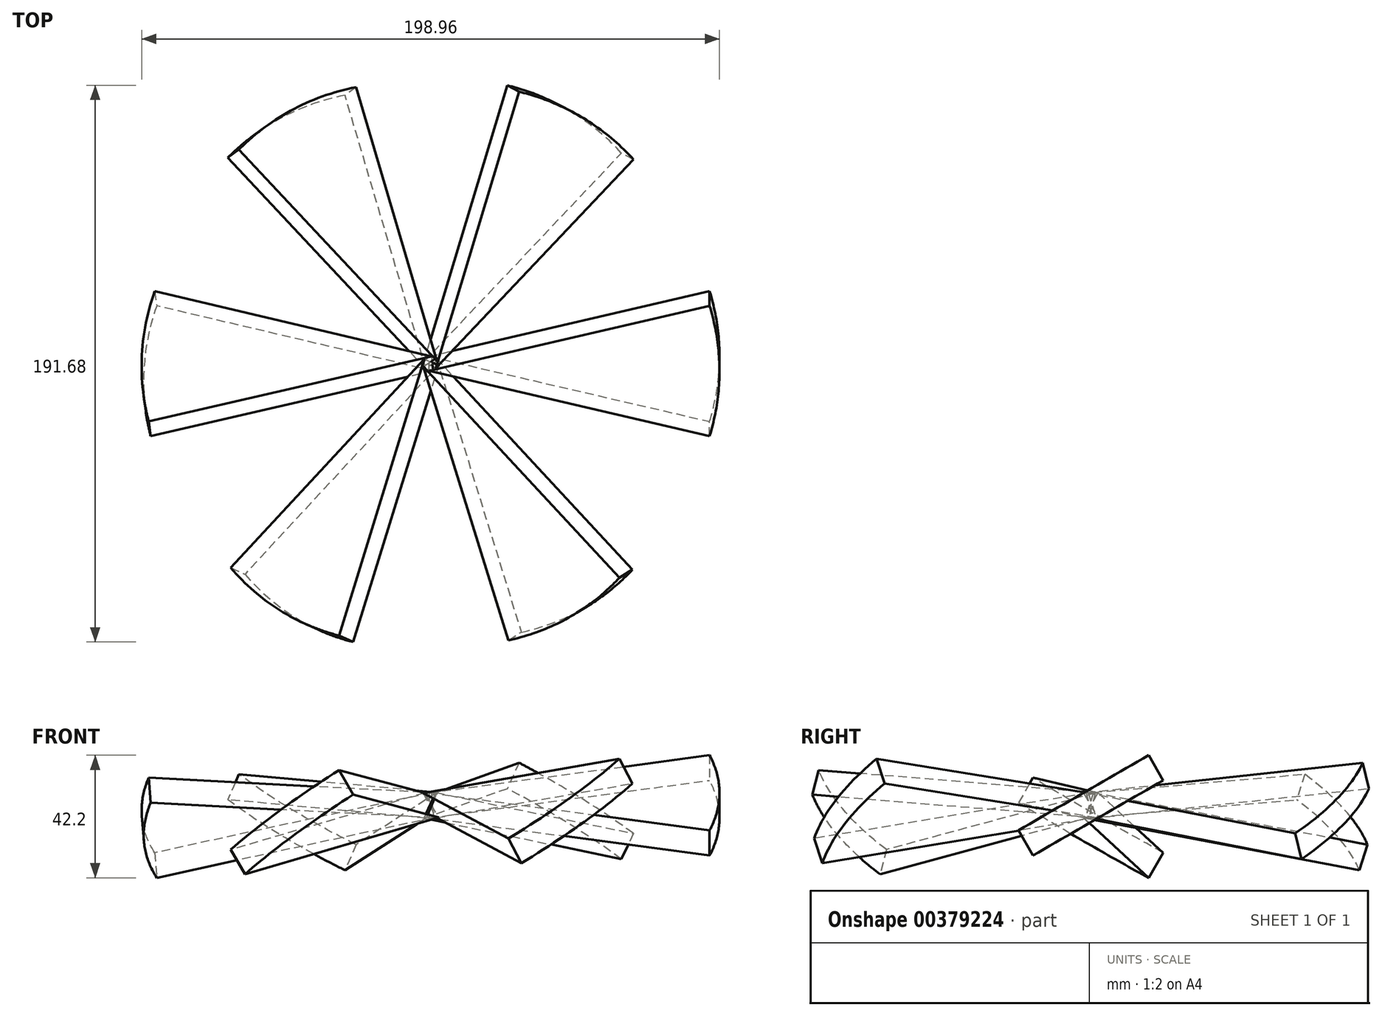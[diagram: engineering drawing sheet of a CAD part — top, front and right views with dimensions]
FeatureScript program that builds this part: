
annotation { "Feature Type Name" : "Feature", "Feature Type Description" : "" }
export const myFeature = defineFeature(function(context is Context, id is Id, definition is map)
    precondition{}
    {
        {
            var Q0;
            Q0=qCreatedBy(makeId("Top.planeOp"),FACE);
            var sketch = newSketch(context, id + "F0", { "sketchPlane" : qUnion([Q0])});
            skLineSegment(sketch, "E0", {"start": v(0, 0) * mm, "end": v(204.54, 0) * mm, "construction": true});
            skLineSegment(sketch, "E1", {"start": v(0, 0) * mm, "end": v(96.6, 25.88) * mm});
            skLineSegment(sketch, "E2", {"start": v(0, 0) * mm, "end": v(96.6, -25.88) * mm});
            skArc(sketch, "E3", {"start": v(96.6, -25.88) * mm, "mid": v(100, 0) * mm, "end": v(96.6, 25.88) * mm});
            skSolve(sketch);
        }
        {
            var Q0;
            Q0=makeQuery(id+"F0.imprint","IMPRINT",FACE,{"disambiguationData":[TD([[makeQuery(id+"F0.imprint","IMPRINT",EDGE,{"derivedFrom":sQuery(id+"F0.wireOp",EDGE,"E1")}),-1.0]])]});
            extrude(context, id + "F1", {"entities" : qUnion([Q0]), "endBound" : BoundingType.SYMMETRIC, "depth" : 10 * mm});
        }
        {
            var Q0;
            Q0=qCreatedBy(makeId("Top.planeOp"),FACE);
            var sketch = newSketch(context, id + "F2", { "sketchPlane" : qUnion([Q0])});
            skLineSegment(sketch, "E4", {"start": v(0, 0) * mm, "end": v(128.98, 0) * mm, "construction": true});
            skSolve(sketch);
        }
        {
            var Q0;
            Q0=makeQuery(id+"F1.opExtrude","SWEPT_BODY",BODY,{"disambiguationData":[OSD([sQuery(id+"F0.wireOp",EDGE,"E1"),sQuery(id+"F0.wireOp",EDGE,"E2"),sQuery(id+"F0.wireOp",EDGE,"E3")])]});
            var Q1;
            Q1=sQuery(id+"F2.wireOp",EDGE,"E4");
            transform(context, id + "F3", {"entities" : qUnion([Q0]), "transformType" : TransformType.ROTATION, "transformAxis" : qUnion([Q1]), "angle" : 30 * degree, "makeCopy" : false});
        }
        {
            var Q0;
            Q0=qCreatedBy(makeId("Front.planeOp"),FACE);
            var sketch = newSketch(context, id + "F4", { "sketchPlane" : qUnion([Q0])});
            skLineSegment(sketch, "E5", {"start": v(0.55, 0.6) * mm, "end": v(0, 14.26) * mm, "construction": true});
            skSolve(sketch);
        }
        {
            var Q0;
            Q0=makeQuery(id+"F1.opExtrude","SWEPT_BODY",BODY,{"disambiguationData":[OSD([sQuery(id+"F0.wireOp",EDGE,"E1"),sQuery(id+"F0.wireOp",EDGE,"E2"),sQuery(id+"F0.wireOp",EDGE,"E3")])]});
            var Q1;
            Q1=sQuery(id+"F4.wireOp",EDGE,"E5");
            circularPattern(context, id + "F5", {"entities" : qUnion([Q0]), "axis" : qUnion([Q1]), "angle" : 360 * degree, "instanceCount" : 6, "equalSpace" : true});
        }
    });
